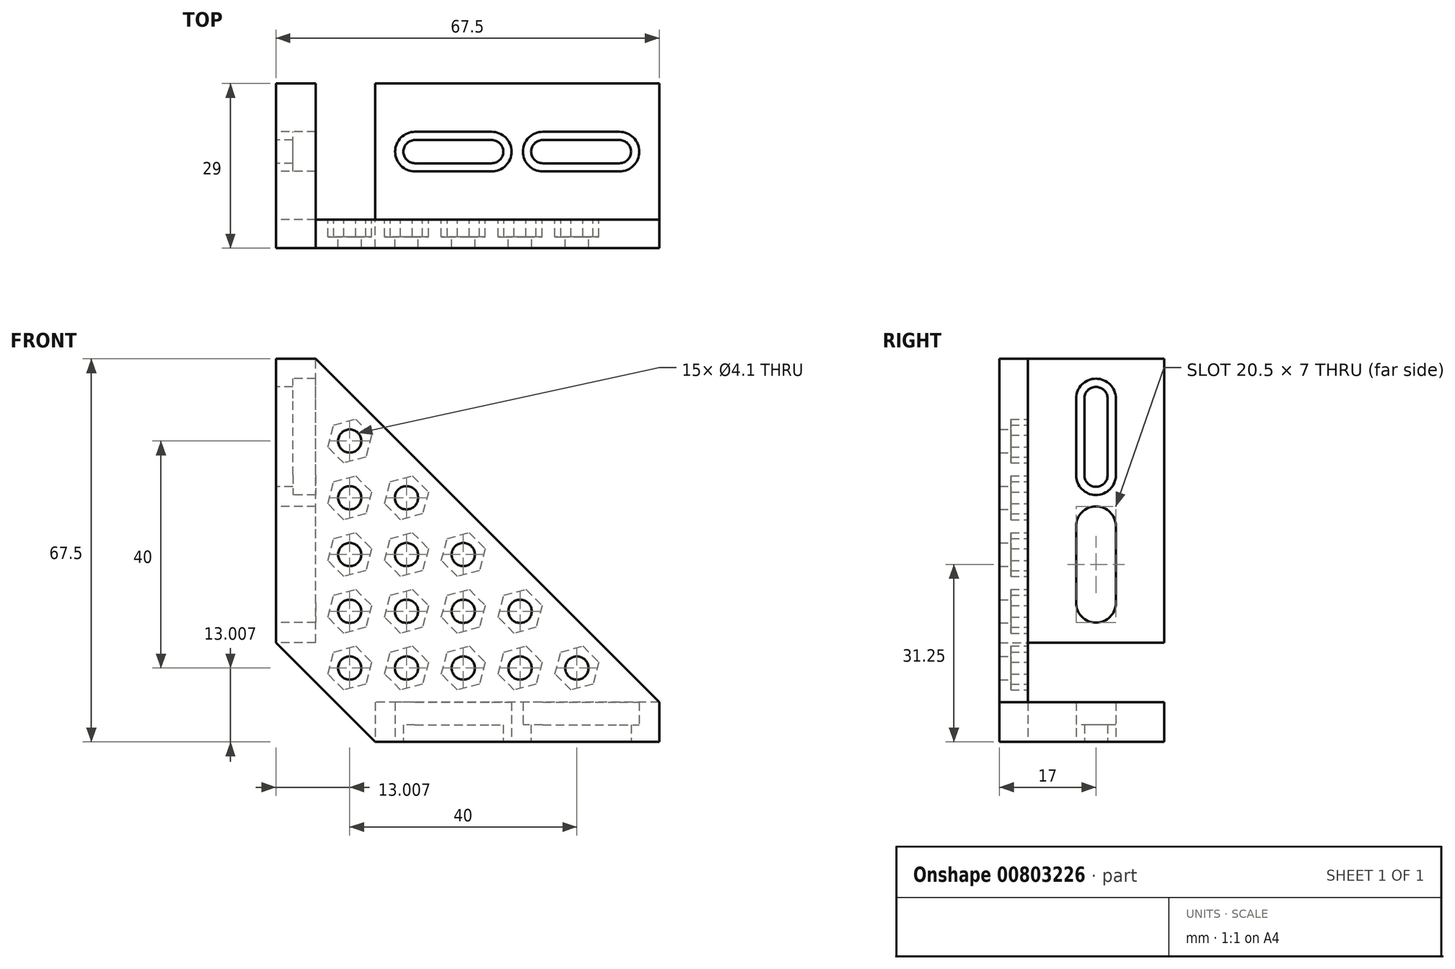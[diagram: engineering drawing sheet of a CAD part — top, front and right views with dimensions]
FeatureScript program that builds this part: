
annotation { "Feature Type Name" : "Feature", "Feature Type Description" : "" }
export const myFeature = defineFeature(function(context is Context, id is Id, definition is map)
    precondition{}
    {
        {
            var Q0;
            Q0=qCreatedBy(makeId("Top.planeOp"),FACE);
            var sketch = newSketch(context, id + "F0", { "sketchPlane" : qUnion([Q0])});
            skLineSegment(sketch, "E0.left", {"start": v(-21, 12) * mm, "end": v(-21, -12) * mm});
            skPoint(sketch, "E0.middle", {"position": v(0, 0) * mm});
            skLineSegment(sketch, "E1", {"start": v(-14, 12) * mm, "end": v(-14, -12) * mm, "construction": true});
            skPoint(sketch, "E2", {"position": v(-14, -8) * mm});
            skPoint(sketch, "E3", {"position": v(0, -8) * mm});
            skPoint(sketch, "E4", {"position": v(-14, 0) * mm});
            skArc(sketch, "E5", {"start": v(-14, -5.95) * mm, "mid": v(-16.05, -8) * mm, "end": v(-14, -10.05) * mm});
            skLineSegment(sketch, "E6", {"start": v(-14, -5.95) * mm, "end": v(0, -5.95) * mm});
            skLineSegment(sketch, "E7.MirrorCS", {"start": v(-14, -10.05) * mm, "end": v(0, -10.05) * mm});
            skArc(sketch, "E8", {"start": v(-14, -2.05) * mm, "mid": v(-16.05, 0) * mm, "end": v(-14, 2.05) * mm});
            skLineSegment(sketch, "E9", {"start": v(-14, -2.05) * mm, "end": v(0, -2.05) * mm});
            skPoint(sketch, "E10.MirrorP", {"position": v(-14, 2.05) * mm});
            skLineSegment(sketch, "E11.MirrorCS", {"start": v(-14, 2.05) * mm, "end": v(0, 2.05) * mm});
            skLineSegment(sketch, "E12.MirrorCS", {"start": v(0, -12) * mm, "end": v(0, 12) * mm, "construction": true});
            skLineSegment(sketch, "E13", {"start": v(-21, -12) * mm, "end": v(0, -12) * mm});
            skLineSegment(sketch, "E14", {"start": v(-21, 0) * mm, "end": v(0, 0) * mm, "construction": true});
            skLineSegment(sketch, "E15", {"start": v(0, -8) * mm, "end": v(-21, -8) * mm, "construction": true});
            skPoint(sketch, "E15.endSnap0", {"position": v(-16.05, -8) * mm});
            skLineSegment(sketch, "E16", {"start": v(0, -12) * mm, "end": v(29, -12) * mm});
            skLineSegment(sketch, "E17", {"start": v(29, -12) * mm, "end": v(29, 12) * mm});
            skLineSegment(sketch, "E18", {"start": v(29, 12) * mm, "end": v(-21, 12) * mm});
            skLineSegment(sketch, "E19", {"start": v(22, 12) * mm, "end": v(22, -12) * mm, "construction": true});
            skLineSegment(sketch, "E20", {"start": v(0, -5.95) * mm, "end": v(22, -5.95) * mm});
            skLineSegment(sketch, "E21", {"start": v(0, -10.05) * mm, "end": v(22, -10.05) * mm});
            skLineSegment(sketch, "E22", {"start": v(22, 0) * mm, "end": v(0, 0) * mm, "construction": true});
            skLineSegment(sketch, "E23", {"start": v(0, -8) * mm, "end": v(22, -8) * mm, "construction": true});
            skArc(sketch, "E24", {"start": v(22, -2.05) * mm, "mid": v(24.05, 0) * mm, "end": v(22, 2.05) * mm});
            skArc(sketch, "E25", {"start": v(22, -10.05) * mm, "mid": v(24.05, -8) * mm, "end": v(22, -5.95) * mm});
            skLineSegment(sketch, "E26.MirrorCS", {"start": v(0, 5.95) * mm, "end": v(22, 5.95) * mm});
            skLineSegment(sketch, "E27.MirrorCS", {"start": v(0, 10.05) * mm, "end": v(22, 10.05) * mm});
            skLineSegment(sketch, "E28.MirrorCS", {"start": v(-14, 10.05) * mm, "end": v(0, 10.05) * mm});
            skLineSegment(sketch, "E29.MirrorCS", {"start": v(-14, 5.95) * mm, "end": v(0, 5.95) * mm});
            skArc(sketch, "E30.MirrorCS", {"start": v(-14, 5.95) * mm, "mid": v(-16.05, 8) * mm, "end": v(-14, 10.05) * mm});
            skArc(sketch, "E31.MirrorCS", {"start": v(22, 10.05) * mm, "mid": v(24.05, 8) * mm, "end": v(22, 5.95) * mm});
            skArc(sketch, "E32.0", {"start": v(-14, -3.5) * mm, "mid": v(-17.5, 0) * mm, "end": v(-14, 3.5) * mm});
            skLineSegment(sketch, "E32.1", {"start": v(2, 3.5) * mm, "end": v(22, 3.5) * mm});
            skArc(sketch, "E32.2", {"start": v(22, -3.5) * mm, "mid": v(25.5, 0) * mm, "end": v(22, 3.5) * mm});
            skLineSegment(sketch, "E32.3", {"start": v(-14, 3.5) * mm, "end": v(2, 3.5) * mm});
            skLineSegment(sketch, "E32.4", {"start": v(2, -3.5) * mm, "end": v(22, -3.5) * mm});
            skLineSegment(sketch, "E32.5", {"start": v(-14, -3.5) * mm, "end": v(2, -3.5) * mm});
            skArc(sketch, "E33.0", {"start": v(-14, -4.5) * mm, "mid": v(-17.5, -8) * mm, "end": v(-14, -11.5) * mm});
            skLineSegment(sketch, "E33.1", {"start": v(2, -4.5) * mm, "end": v(22, -4.5) * mm});
            skArc(sketch, "E33.2", {"start": v(22, -11.5) * mm, "mid": v(25.5, -8) * mm, "end": v(22, -4.5) * mm});
            skLineSegment(sketch, "E33.3", {"start": v(-14, -4.5) * mm, "end": v(2, -4.5) * mm});
            skLineSegment(sketch, "E33.4", {"start": v(2, -11.5) * mm, "end": v(22, -11.5) * mm});
            skLineSegment(sketch, "E33.5", {"start": v(-14, -11.5) * mm, "end": v(2, -11.5) * mm});
            skArc(sketch, "E34.0", {"start": v(-14, 4.5) * mm, "mid": v(-17.5, 8) * mm, "end": v(-14, 11.5) * mm});
            skLineSegment(sketch, "E34.1", {"start": v(0, 11.5) * mm, "end": v(22, 11.5) * mm});
            skArc(sketch, "E34.2", {"start": v(22, 11.5) * mm, "mid": v(25.5, 8) * mm, "end": v(22, 4.5) * mm});
            skLineSegment(sketch, "E34.3", {"start": v(-14, 11.5) * mm, "end": v(0, 11.5) * mm});
            skLineSegment(sketch, "E34.4", {"start": v(0, 4.5) * mm, "end": v(22, 4.5) * mm});
            skLineSegment(sketch, "E34.5", {"start": v(-14, 4.5) * mm, "end": v(0, 4.5) * mm});
            skLineSegment(sketch, "E35", {"start": v(4, 12) * mm, "end": v(4, -12) * mm, "construction": true});
            skPoint(sketch, "E36", {"position": v(-0.5, 0) * mm});
            skPoint(sketch, "E37", {"position": v(8.5, 0) * mm});
            skArc(sketch, "E38", {"start": v(-0.5, -3.5) * mm, "mid": v(3, 0) * mm, "end": v(-0.5, 3.5) * mm});
            skArc(sketch, "E39", {"start": v(-0.5, -2.05) * mm, "mid": v(1.55, 0) * mm, "end": v(-0.5, 2.05) * mm});
            skArc(sketch, "E40", {"start": v(8.5, -3.5) * mm, "mid": v(5, 0) * mm, "end": v(8.5, 3.5) * mm});
            skArc(sketch, "E41", {"start": v(8.5, -2.05) * mm, "mid": v(6.45, 0) * mm, "end": v(8.5, 2.05) * mm});
            skPoint(sketch, "E42", {"position": v(1.55, 0) * mm});
            skPoint(sketch, "E43", {"position": v(3, 0) * mm});
            skPoint(sketch, "E44", {"position": v(5, 0) * mm});
            skPoint(sketch, "E45", {"position": v(6.45, 0) * mm});
            skLineSegment(sketch, "E46", {"start": v(8.5, -2.05) * mm, "end": v(22, -2.05) * mm});
            skLineSegment(sketch, "E47", {"start": v(8.5, 2.05) * mm, "end": v(22, 2.05) * mm});
            skSolve(sketch);
        }
        {
            var Q0;
            Q0=makeQuery(id+"F0.imprint","IMPRINT",FACE,{"disambiguationData":[TD([[makeQuery(id+"F0.imprint","IMPRINT",EDGE,{"derivedFrom":sQuery(id+"F0.wireOp",EDGE,"E0.left")}),1.0]])]});
            var Q1;
            Q1=makeQuery(id+"F0.imprint","IMPRINT",FACE,{"disambiguationData":[TD([[makeQuery(id+"F0.imprint","IMPRINT",EDGE,{"derivedFrom":sQuery(id+"F0.wireOp",EDGE,"E5")}),1.0]])]});
            var Q2;
            Q2=makeQuery(id+"F0.imprint","IMPRINT",FACE,{"disambiguationData":[TD([[makeQuery(id+"F0.imprint","IMPRINT",EDGE,{"derivedFrom":sQuery(id+"F0.wireOp",EDGE,"E5")}),-1.0]])]});
            var Q3;
            Q3=makeQuery(id+"F0.imprint","IMPRINT",FACE,{"disambiguationData":[TD([[makeQuery(id+"F0.imprint","IMPRINT",EDGE,{"derivedFrom":sQuery(id+"F0.wireOp",EDGE,"E26.MirrorCS")}),-1.0]])]});
            var Q4;
            Q4=makeQuery(id+"F0.imprint","IMPRINT",FACE,{"disambiguationData":[TD([[makeQuery(id+"F0.imprint","IMPRINT",EDGE,{"derivedFrom":sQuery(id+"F0.wireOp",EDGE,"E26.MirrorCS")}),1.0]])]});
            var Q5;
            {var subQ3=sQuery(id+"F0.wireOp",EDGE,"E38");Q5=makeQuery(id+"F0.imprint","IMPRINT",FACE,{"disambiguationData":[TD([[makeQuery(id+"F0.imprint","IMPRINT",EDGE,{"derivedFrom":subQ3}),-1.0]])]});}
            extrude(context, id + "F1", {"entities" : qUnion([Q0, Q1, Q2, Q3, Q4, Q5]), "depth" : 7 * mm, "offsetDistance" : 25 * mm});
        }
        {
            var Q0;
            Q0=makeQuery(id+"F0.imprint","IMPRINT",FACE,{"disambiguationData":[TD([[makeQuery(id+"F0.imprint","IMPRINT",EDGE,{"derivedFrom":sQuery(id+"F0.wireOp",EDGE,"E8")}),1.0]])]});
            var Q1;
            Q1=makeQuery(id+"F0.imprint","IMPRINT",FACE,{"disambiguationData":[TD([[makeQuery(id+"F0.imprint","IMPRINT",EDGE,{"derivedFrom":sQuery(id+"F0.wireOp",EDGE,"E24")}),-1.0]])]});
            extrude(context, id + "F2", {"entities" : qUnion([Q0, Q1]), "operationType" : NewBodyOperationType.ADD, "depth" : 3 * mm, "offsetDistance" : 25 * mm});
        }
        {
            var Q0;
            Q0=makeQuery(id+"F1.opExtrude","SWEPT_FACE",FACE,{"disambiguationData":[OSD([sQuery(id+"F0.wireOp",EDGE,"E0.left")])]});
            var sketch = newSketch(context, id + "F3", { "sketchPlane" : qUnion([Q0])});
            skLineSegment(sketch, "E48", {"start": v(-12, 3.5) * mm, "end": v(12, 3.5) * mm, "construction": true});
            skSolve(sketch);
        }
        {
            var Q0;
            Q0=makeQuery(id+"F1.opExtrude","SWEPT_BODY",BODY,{"disambiguationData":[OSD([sQuery(id+"F0.wireOp",EDGE,"E0.bottom"),sQuery(id+"F0.wireOp",EDGE,"E0.top"),sQuery(id+"F0.wireOp",EDGE,"E0.left"),sQuery(id+"F0.wireOp",EDGE,"E0.right"),sQuery(id+"F0.wireOp",EDGE,"rf366HtQ-3S43-huQP-rZQL-GLvETnePYKPt"),sQuery(id+"F0.wireOp",EDGE,"72d57c59-205e-4b86-9b7f-fefa83471a3c0.MirrorC"),sQuery(id+"F0.wireOp",EDGE,"3BxVGwLA-TLUy-tZVP-cH0U-NxRYkcQ5ksQi"),sQuery(id+"F0.wireOp",EDGE,"b526d6a5-a937-4610-9a53-f8e406b30c9d0.MirrorC"),sQuery(id+"F0.wireOp",EDGE,"71981b63-6e51-433c-862b-60b74b25135c0.MirrorC"),sQuery(id+"F0.wireOp",EDGE,"b5f8f83e-67df-48da-9f18-6f8bbd20fa1b0.MirrorC"),sQuery(id+"F0.wireOp",EDGE,"1DxgEhBs-8iCY-IMLj-HmtB-05ri525AO9wY"),sQuery(id+"F0.wireOp",EDGE,"NxLUD5A4-VjtB-lD8M-x3iM-VxBEk0lLSaKk"),sQuery(id+"F0.wireOp",EDGE,"3f1f5e11-1e70-4af8-87df-d7b5c765f6460.MirrorC")])]});
            var Q1;
            Q1=sQuery(id+"F3.wireOp",EDGE,"E48");
            transform(context, id + "F4", {"entities" : qUnion([Q0]), "transformType" : TransformType.ROTATION, "transformAxis" : qUnion([Q1]), "angle" : 90 * degree, "makeCopy" : true});
        }
        {
            var Q0;
            Q0=makeQuery(id+"F4.opPattern","COPY",FACE,{"derivedFrom":makeQuery(id+"F1.opExtrude","SWEPT_FACE",FACE,{"disambiguationData":[OSD([sQuery(id+"F0.wireOp",EDGE,"E0.left")])]}),"instanceName":"1"});
            var sketch = newSketch(context, id + "F5", { "sketchPlane" : qUnion([Q0])});
            skLineSegment(sketch, "E49", {"start": v(-21, -12) * mm, "end": v(-21, 12) * mm, "construction": true});
            skPoint(sketch, "E49.startSnap0", {"position": v(-21, -12) * mm});
            skSolve(sketch);
        }
        {
            var Q0;
            Q0=sQuery(id+"F5.wireOp",EDGE,"E49");
            cPlane(context, id + "F6", {"entities" : qUnion([Q0]), "cplaneType" : CPlaneType.LINE_ANGLE, "offset" : 25 * mm, "angle" : 90 * degree, "width" : 150 * mm, "height" : 150 * mm});
        }
        {
            var Q0;
            Q0=qCreatedBy(id+"F6.planeOp",FACE);
            var sketch = newSketch(context, id + "F7", { "sketchPlane" : qUnion([Q0])});
            skLineSegment(sketch, "E50", {"start": v(0, 3.5) * mm, "end": v(0, 53.5) * mm, "construction": true});
            skSolve(sketch);
        }
        {
            var Q0;
            Q0=makeQuery(id+"F4.opPattern","COPY",BODY,{"derivedFrom":makeQuery(id+"F1.opExtrude","SWEPT_BODY",BODY,{"disambiguationData":[OSD([sQuery(id+"F0.wireOp",EDGE,"E0.left"),sQuery(id+"F0.wireOp",EDGE,"E13"),sQuery(id+"F0.wireOp",EDGE,"E16"),sQuery(id+"F0.wireOp",EDGE,"E17"),sQuery(id+"F0.wireOp",EDGE,"E18"),sQuery(id+"F0.wireOp",EDGE,"E32.0"),sQuery(id+"F0.wireOp",EDGE,"E32.1"),sQuery(id+"F0.wireOp",EDGE,"E32.2"),sQuery(id+"F0.wireOp",EDGE,"E32.3"),sQuery(id+"F0.wireOp",EDGE,"E32.4"),sQuery(id+"F0.wireOp",EDGE,"E32.5")])]}),"instanceName":"1"});
            var Q1;
            Q1=sQuery(id+"F7.wireOp",EDGE,"E50");
            transform(context, id + "F8", {"entities" : qUnion([Q0]), "transformType" : TransformType.ROTATION, "transformAxis" : qUnion([Q1]), "angle" : 180 * degree, "makeCopy" : false});
        }
        {
            var Q0;
            Q0=makeQuery(id+"F4.opPattern","COPY",BODY,{"derivedFrom":makeQuery(id+"F1.opExtrude","SWEPT_BODY",BODY,{"disambiguationData":[OSD([sQuery(id+"F0.wireOp",EDGE,"E0.bottom"),sQuery(id+"F0.wireOp",EDGE,"E0.top"),sQuery(id+"F0.wireOp",EDGE,"E0.left"),sQuery(id+"F0.wireOp",EDGE,"E0.right"),sQuery(id+"F0.wireOp",EDGE,"rf366HtQ-3S43-huQP-rZQL-GLvETnePYKPt"),sQuery(id+"F0.wireOp",EDGE,"72d57c59-205e-4b86-9b7f-fefa83471a3c0.MirrorC"),sQuery(id+"F0.wireOp",EDGE,"3BxVGwLA-TLUy-tZVP-cH0U-NxRYkcQ5ksQi"),sQuery(id+"F0.wireOp",EDGE,"b526d6a5-a937-4610-9a53-f8e406b30c9d0.MirrorC"),sQuery(id+"F0.wireOp",EDGE,"71981b63-6e51-433c-862b-60b74b25135c0.MirrorC"),sQuery(id+"F0.wireOp",EDGE,"b5f8f83e-67df-48da-9f18-6f8bbd20fa1b0.MirrorC"),sQuery(id+"F0.wireOp",EDGE,"1DxgEhBs-8iCY-IMLj-HmtB-05ri525AO9wY"),sQuery(id+"F0.wireOp",EDGE,"NxLUD5A4-VjtB-lD8M-x3iM-VxBEk0lLSaKk"),sQuery(id+"F0.wireOp",EDGE,"3f1f5e11-1e70-4af8-87df-d7b5c765f6460.MirrorC")])]}),"instanceName":"1"});
            var Q1;
            Q1=qCreatedBy(makeId("Top.planeOp"),FACE);
            transform(context, id + "F9", {"entities" : qUnion([Q0]), "transformType" : TransformType.TRANSLATION_DISTANCE, "transformDirection" : qUnion([Q1]), "distance" : 14 * mm, "makeCopy" : false});
        }
        {
            var Q0;
            Q0=makeQuery(id+"F4.opPattern","COPY",BODY,{"derivedFrom":makeQuery(id+"F1.opExtrude","SWEPT_BODY",BODY,{"disambiguationData":[OSD([sQuery(id+"F0.wireOp",EDGE,"E0.bottom"),sQuery(id+"F0.wireOp",EDGE,"E0.top"),sQuery(id+"F0.wireOp",EDGE,"E0.left"),sQuery(id+"F0.wireOp",EDGE,"E0.right"),sQuery(id+"F0.wireOp",EDGE,"rf366HtQ-3S43-huQP-rZQL-GLvETnePYKPt"),sQuery(id+"F0.wireOp",EDGE,"72d57c59-205e-4b86-9b7f-fefa83471a3c0.MirrorC"),sQuery(id+"F0.wireOp",EDGE,"3BxVGwLA-TLUy-tZVP-cH0U-NxRYkcQ5ksQi"),sQuery(id+"F0.wireOp",EDGE,"b526d6a5-a937-4610-9a53-f8e406b30c9d0.MirrorC"),sQuery(id+"F0.wireOp",EDGE,"71981b63-6e51-433c-862b-60b74b25135c0.MirrorC"),sQuery(id+"F0.wireOp",EDGE,"b5f8f83e-67df-48da-9f18-6f8bbd20fa1b0.MirrorC"),sQuery(id+"F0.wireOp",EDGE,"1DxgEhBs-8iCY-IMLj-HmtB-05ri525AO9wY"),sQuery(id+"F0.wireOp",EDGE,"NxLUD5A4-VjtB-lD8M-x3iM-VxBEk0lLSaKk"),sQuery(id+"F0.wireOp",EDGE,"3f1f5e11-1e70-4af8-87df-d7b5c765f6460.MirrorC")])]}),"instanceName":"1"});
            var Q1;
            Q1=qCreatedBy(makeId("Right.planeOp"),FACE);
            transform(context, id + "F10", {"entities" : qUnion([Q0]), "transformType" : TransformType.TRANSLATION_DISTANCE, "transformDirection" : qUnion([Q1]), "distance" : 14 * mm, "oppositeDirection" : true, "makeCopy" : false});
        }
        {
            var Q0;
            Q0=sQuery(id+"F0.wireOp",VERTEX,"E0.left.end");
            var Q1;
            Q1=makeQuery(id+"F4.opPattern","COPY",VERTEX,{"derivedFrom":makeQuery(id+"F1.opExtrude","CAP_VERTEX",VERTEX,{"disambiguationData":[OSD([sQuery(id+"F0.wireOp",EDGE,"E0.left"),sQuery(id+"F0.wireOp",EDGE,"E18")])],"isStart":true}),"instanceName":"1"});
            var Q2;
            Q2=makeQuery(id+"F4.opPattern","COPY",VERTEX,{"derivedFrom":makeQuery(id+"F1.opExtrude","CAP_VERTEX",VERTEX,{"disambiguationData":[OSD([sQuery(id+"F0.wireOp",EDGE,"E0.left"),sQuery(id+"F0.wireOp",EDGE,"E18")])],"isStart":false}),"instanceName":"1"});
            cPlane(context, id + "F11", {"entities" : qUnion([Q0, Q1, Q2]), "cplaneType" : CPlaneType.THREE_POINT, "offset" : 25 * mm, "width" : 150 * mm, "height" : 150 * mm});
        }
        {
            var Q0;
            Q0=qCreatedBy(id+"F11.planeOp",FACE);
            var sketch = newSketch(context, id + "F12", { "sketchPlane" : qUnion([Q0])});
            skLineSegment(sketch, "E51", {"start": v(-21, 0) * mm, "end": v(-38.5, 17.5) * mm});
            skLineSegment(sketch, "E52", {"start": v(-31.5, 67.5) * mm, "end": v(29, 7) * mm});
            skLineSegment(sketch, "E53", {"start": v(-38.5, 17.5) * mm, "end": v(-38.5, 67.5) * mm});
            skLineSegment(sketch, "E54", {"start": v(-31.5, 67.5) * mm, "end": v(-38.5, 67.5) * mm});
            skLineSegment(sketch, "E55", {"start": v(-21, 0) * mm, "end": v(29, 0) * mm});
            skLineSegment(sketch, "E56", {"start": v(29, 0) * mm, "end": v(29, 7) * mm});
            skLineSegment(sketch, "E57", {"start": v(-38.5, 67.5) * mm, "end": v(-31.5, 67.5) * mm});
            skPoint(sketch, "E58", {"position": v(-5.5, 33) * mm});
            skCircle(sketch, "E59", {"center": v(-5.5, 33) * mm, "radius": 2.05 * mm});
            skCircle(sketch, "E60.cCircle", {"center": v(-5.5, 33) * mm, "radius": 4 * mm, "construction": true});
            skLineSegment(sketch, "E60.0", {"start": v(-8.32, 35.84) * mm, "end": v(-4.46, 36.87) * mm});
            skLineSegment(sketch, "E60.1", {"start": v(-4.46, 36.87) * mm, "end": v(-1.63, 34.04) * mm});
            skLineSegment(sketch, "E60.2", {"start": v(-1.63, 34.04) * mm, "end": v(-2.66, 30.18) * mm});
            skLineSegment(sketch, "E60.3", {"start": v(-2.66, 30.18) * mm, "end": v(-6.53, 29.14) * mm});
            skLineSegment(sketch, "E60.4", {"start": v(-6.53, 29.14) * mm, "end": v(-9.36, 31.97) * mm});
            skLineSegment(sketch, "E60.5", {"start": v(-9.36, 31.97) * mm, "end": v(-8.32, 35.84) * mm});
            skLineSegment(sketch, "E61", {"start": v(-29.75, 8.75) * mm, "end": v(-1.25, 37.25) * mm, "construction": true});
            skLineSegment(sketch, "E62", {"start": v(-38.5, 17.5) * mm, "end": v(-38.5, 0) * mm, "construction": true});
            skLineSegment(sketch, "E63", {"start": v(-38.5, 0) * mm, "end": v(-21, 0) * mm, "construction": true});
            skLineSegment(sketch, "E64", {"start": v(-21, 7) * mm, "end": v(-38.5, 7) * mm, "construction": true});
            skLineSegment(sketch, "E65", {"start": v(-38.5, 7) * mm, "end": v(-38.5, 17.5) * mm, "construction": true});
            skLineSegment(sketch, "E66", {"start": v(-23.5, 59.5) * mm, "end": v(-23.5, 15) * mm, "construction": true});
            skLineSegment(sketch, "E67", {"start": v(-23.5, 15) * mm, "end": v(21, 15) * mm, "construction": true});
            skPoint(sketch, "E68", {"position": v(-2.66, 35.84) * mm});
            skLineSegment(sketch, "E69", {"start": v(-5.5, 33) * mm, "end": v(-5.5, 15) * mm, "construction": true});
            skLineSegment(sketch, "E70", {"start": v(-5.5, 33) * mm, "end": v(-23.5, 33) * mm, "construction": true});
            skPoint(sketch, "E71", {"position": v(-5.5, 23) * mm});
            skCircle(sketch, "E72", {"center": v(-5.5, 23) * mm, "radius": 2.05 * mm});
            skCircle(sketch, "E73.cCircle", {"center": v(-5.5, 23) * mm, "radius": 4 * mm, "construction": true});
            skLineSegment(sketch, "E73.0", {"start": v(-8.32, 25.84) * mm, "end": v(-4.46, 26.87) * mm});
            skLineSegment(sketch, "E73.1", {"start": v(-4.46, 26.87) * mm, "end": v(-1.63, 24.04) * mm});
            skLineSegment(sketch, "E73.2", {"start": v(-1.63, 24.04) * mm, "end": v(-2.66, 20.18) * mm});
            skLineSegment(sketch, "E73.3", {"start": v(-2.66, 20.18) * mm, "end": v(-6.53, 19.14) * mm});
            skLineSegment(sketch, "E73.4", {"start": v(-6.53, 19.14) * mm, "end": v(-9.36, 21.97) * mm});
            skLineSegment(sketch, "E73.5", {"start": v(-9.36, 21.97) * mm, "end": v(-8.32, 25.84) * mm});
            skPoint(sketch, "E74", {"position": v(-15.5, 33) * mm});
            skCircle(sketch, "E75", {"center": v(-15.5, 33) * mm, "radius": 2.05 * mm});
            skCircle(sketch, "E76.cCircle", {"center": v(-15.5, 33) * mm, "radius": 4 * mm, "construction": true});
            skLineSegment(sketch, "E76.0", {"start": v(-18.32, 35.84) * mm, "end": v(-14.46, 36.87) * mm});
            skLineSegment(sketch, "E76.1", {"start": v(-14.46, 36.87) * mm, "end": v(-11.63, 34.04) * mm});
            skLineSegment(sketch, "E76.2", {"start": v(-11.63, 34.04) * mm, "end": v(-12.66, 30.18) * mm});
            skLineSegment(sketch, "E76.3", {"start": v(-12.66, 30.18) * mm, "end": v(-16.53, 29.14) * mm});
            skLineSegment(sketch, "E76.4", {"start": v(-16.53, 29.14) * mm, "end": v(-19.36, 31.97) * mm});
            skLineSegment(sketch, "E76.5", {"start": v(-19.36, 31.97) * mm, "end": v(-18.32, 35.84) * mm});
            skPoint(sketch, "E77", {"position": v(-15.5, 23) * mm});
            skCircle(sketch, "E78", {"center": v(-15.5, 23) * mm, "radius": 2.05 * mm});
            skCircle(sketch, "E79.cCircle", {"center": v(-15.5, 23) * mm, "radius": 4 * mm, "construction": true});
            skLineSegment(sketch, "E79.0", {"start": v(-18.32, 25.84) * mm, "end": v(-14.46, 26.87) * mm});
            skLineSegment(sketch, "E79.1", {"start": v(-14.46, 26.87) * mm, "end": v(-11.63, 24.04) * mm});
            skLineSegment(sketch, "E79.2", {"start": v(-11.63, 24.04) * mm, "end": v(-12.66, 20.18) * mm});
            skLineSegment(sketch, "E79.3", {"start": v(-12.66, 20.18) * mm, "end": v(-16.53, 19.14) * mm});
            skLineSegment(sketch, "E79.4", {"start": v(-16.53, 19.14) * mm, "end": v(-19.36, 21.97) * mm});
            skLineSegment(sketch, "E79.5", {"start": v(-19.36, 21.97) * mm, "end": v(-18.32, 25.84) * mm});
            skLineSegment(sketch, "E80", {"start": v(-5.5, 23) * mm, "end": v(13, 23) * mm, "construction": true});
            skLineSegment(sketch, "E81", {"start": v(-15.5, 33) * mm, "end": v(-15.5, 51.5) * mm, "construction": true});
            skPoint(sketch, "E82", {"position": v(4.5, 23) * mm});
            skCircle(sketch, "E83", {"center": v(4.5, 23) * mm, "radius": 2.05 * mm});
            skCircle(sketch, "E84.cCircle", {"center": v(4.5, 23) * mm, "radius": 4 * mm, "construction": true});
            skLineSegment(sketch, "E84.0", {"start": v(1.68, 25.84) * mm, "end": v(5.54, 26.87) * mm});
            skLineSegment(sketch, "E84.1", {"start": v(5.54, 26.87) * mm, "end": v(8.37, 24.04) * mm});
            skLineSegment(sketch, "E84.2", {"start": v(8.37, 24.04) * mm, "end": v(7.34, 20.18) * mm});
            skLineSegment(sketch, "E84.3", {"start": v(7.34, 20.18) * mm, "end": v(3.47, 19.14) * mm});
            skLineSegment(sketch, "E84.4", {"start": v(3.47, 19.14) * mm, "end": v(0.64, 21.97) * mm});
            skLineSegment(sketch, "E84.5", {"start": v(0.64, 21.97) * mm, "end": v(1.68, 25.84) * mm});
            skPoint(sketch, "E85", {"position": v(-15.5, 43) * mm});
            skCircle(sketch, "E86", {"center": v(-15.5, 43) * mm, "radius": 2.05 * mm});
            skCircle(sketch, "E87.cCircle", {"center": v(-15.5, 43) * mm, "radius": 4 * mm, "construction": true});
            skLineSegment(sketch, "E87.0", {"start": v(-18.32, 45.84) * mm, "end": v(-14.46, 46.87) * mm});
            skLineSegment(sketch, "E87.1", {"start": v(-14.46, 46.87) * mm, "end": v(-11.63, 44.04) * mm});
            skLineSegment(sketch, "E87.2", {"start": v(-11.63, 44.04) * mm, "end": v(-12.66, 40.18) * mm});
            skLineSegment(sketch, "E87.3", {"start": v(-12.66, 40.18) * mm, "end": v(-16.53, 39.14) * mm});
            skLineSegment(sketch, "E87.4", {"start": v(-16.53, 39.14) * mm, "end": v(-19.36, 41.97) * mm});
            skLineSegment(sketch, "E87.5", {"start": v(-19.36, 41.97) * mm, "end": v(-18.32, 45.84) * mm});
            skPoint(sketch, "E88", {"position": v(-25.5, 33) * mm});
            skCircle(sketch, "E89", {"center": v(-25.5, 33) * mm, "radius": 2.05 * mm});
            skCircle(sketch, "E90.cCircle", {"center": v(-25.5, 33) * mm, "radius": 4 * mm, "construction": true});
            skLineSegment(sketch, "E90.0", {"start": v(-28.32, 35.84) * mm, "end": v(-24.46, 36.87) * mm});
            skLineSegment(sketch, "E90.1", {"start": v(-24.46, 36.87) * mm, "end": v(-21.63, 34.04) * mm});
            skLineSegment(sketch, "E90.2", {"start": v(-21.63, 34.04) * mm, "end": v(-22.66, 30.18) * mm});
            skLineSegment(sketch, "E90.3", {"start": v(-22.66, 30.18) * mm, "end": v(-26.53, 29.14) * mm});
            skLineSegment(sketch, "E90.4", {"start": v(-26.53, 29.14) * mm, "end": v(-29.36, 31.97) * mm});
            skLineSegment(sketch, "E90.5", {"start": v(-29.36, 31.97) * mm, "end": v(-28.32, 35.84) * mm});
            skPoint(sketch, "E91", {"position": v(-25.5, 23) * mm});
            skCircle(sketch, "E92", {"center": v(-25.5, 23) * mm, "radius": 2.05 * mm});
            skCircle(sketch, "E93.cCircle", {"center": v(-25.5, 23) * mm, "radius": 4 * mm, "construction": true});
            skLineSegment(sketch, "E93.0", {"start": v(-28.32, 25.84) * mm, "end": v(-24.46, 26.87) * mm});
            skLineSegment(sketch, "E93.1", {"start": v(-24.46, 26.87) * mm, "end": v(-21.63, 24.04) * mm});
            skLineSegment(sketch, "E93.2", {"start": v(-21.63, 24.04) * mm, "end": v(-22.66, 20.18) * mm});
            skLineSegment(sketch, "E93.3", {"start": v(-22.66, 20.18) * mm, "end": v(-26.53, 19.14) * mm});
            skLineSegment(sketch, "E93.4", {"start": v(-26.53, 19.14) * mm, "end": v(-29.36, 21.97) * mm});
            skLineSegment(sketch, "E93.5", {"start": v(-29.36, 21.97) * mm, "end": v(-28.32, 25.84) * mm});
            skPoint(sketch, "E94", {"position": v(-25.5, 43) * mm});
            skCircle(sketch, "E95", {"center": v(-25.5, 43) * mm, "radius": 2.05 * mm});
            skCircle(sketch, "E96.cCircle", {"center": v(-25.5, 43) * mm, "radius": 4 * mm, "construction": true});
            skLineSegment(sketch, "E96.0", {"start": v(-28.32, 45.84) * mm, "end": v(-24.46, 46.87) * mm});
            skLineSegment(sketch, "E96.1", {"start": v(-24.46, 46.87) * mm, "end": v(-21.63, 44.04) * mm});
            skLineSegment(sketch, "E96.2", {"start": v(-21.63, 44.04) * mm, "end": v(-22.66, 40.18) * mm});
            skLineSegment(sketch, "E96.3", {"start": v(-22.66, 40.18) * mm, "end": v(-26.53, 39.14) * mm});
            skLineSegment(sketch, "E96.4", {"start": v(-26.53, 39.14) * mm, "end": v(-29.36, 41.97) * mm});
            skLineSegment(sketch, "E96.5", {"start": v(-29.36, 41.97) * mm, "end": v(-28.32, 45.84) * mm});
            skLineSegment(sketch, "E97", {"start": v(-25.5, 61.5) * mm, "end": v(-25.5, 13) * mm, "construction": true});
            skPoint(sketch, "E98", {"position": v(-5.5, 13) * mm});
            skCircle(sketch, "E99", {"center": v(-5.5, 13) * mm, "radius": 2.05 * mm});
            skCircle(sketch, "E100.cCircle", {"center": v(-5.5, 13) * mm, "radius": 4 * mm, "construction": true});
            skLineSegment(sketch, "E100.0", {"start": v(-8.32, 15.84) * mm, "end": v(-4.46, 16.87) * mm});
            skLineSegment(sketch, "E100.1", {"start": v(-4.46, 16.87) * mm, "end": v(-1.63, 14.04) * mm});
            skLineSegment(sketch, "E100.2", {"start": v(-1.63, 14.04) * mm, "end": v(-2.66, 10.18) * mm});
            skLineSegment(sketch, "E100.3", {"start": v(-2.66, 10.18) * mm, "end": v(-6.53, 9.14) * mm});
            skLineSegment(sketch, "E100.4", {"start": v(-6.53, 9.14) * mm, "end": v(-9.36, 11.97) * mm});
            skLineSegment(sketch, "E100.5", {"start": v(-9.36, 11.97) * mm, "end": v(-8.32, 15.84) * mm});
            skPoint(sketch, "E101", {"position": v(-15.5, 13) * mm});
            skCircle(sketch, "E102", {"center": v(-15.5, 13) * mm, "radius": 2.05 * mm});
            skCircle(sketch, "E103.cCircle", {"center": v(-15.5, 13) * mm, "radius": 4 * mm, "construction": true});
            skLineSegment(sketch, "E103.0", {"start": v(-18.32, 15.84) * mm, "end": v(-14.46, 16.87) * mm});
            skLineSegment(sketch, "E103.1", {"start": v(-14.46, 16.87) * mm, "end": v(-11.63, 14.04) * mm});
            skLineSegment(sketch, "E103.2", {"start": v(-11.63, 14.04) * mm, "end": v(-12.66, 10.18) * mm});
            skLineSegment(sketch, "E103.3", {"start": v(-12.66, 10.18) * mm, "end": v(-16.53, 9.14) * mm});
            skLineSegment(sketch, "E103.4", {"start": v(-16.53, 9.14) * mm, "end": v(-19.36, 11.97) * mm});
            skLineSegment(sketch, "E103.5", {"start": v(-19.36, 11.97) * mm, "end": v(-18.32, 15.84) * mm});
            skPoint(sketch, "E104", {"position": v(4.5, 13) * mm});
            skCircle(sketch, "E105", {"center": v(4.5, 13) * mm, "radius": 2.05 * mm});
            skCircle(sketch, "E106.cCircle", {"center": v(4.5, 13) * mm, "radius": 4 * mm, "construction": true});
            skLineSegment(sketch, "E106.0", {"start": v(1.68, 15.84) * mm, "end": v(5.54, 16.87) * mm});
            skLineSegment(sketch, "E106.1", {"start": v(5.54, 16.87) * mm, "end": v(8.37, 14.04) * mm});
            skLineSegment(sketch, "E106.2", {"start": v(8.37, 14.04) * mm, "end": v(7.34, 10.18) * mm});
            skLineSegment(sketch, "E106.3", {"start": v(7.34, 10.18) * mm, "end": v(3.47, 9.14) * mm});
            skLineSegment(sketch, "E106.4", {"start": v(3.47, 9.14) * mm, "end": v(0.64, 11.97) * mm});
            skLineSegment(sketch, "E106.5", {"start": v(0.64, 11.97) * mm, "end": v(1.68, 15.84) * mm});
            skPoint(sketch, "E107", {"position": v(-25.5, 13) * mm});
            skCircle(sketch, "E108", {"center": v(-25.5, 13) * mm, "radius": 2.05 * mm});
            skCircle(sketch, "E109.cCircle", {"center": v(-25.5, 13) * mm, "radius": 4 * mm, "construction": true});
            skLineSegment(sketch, "E109.0", {"start": v(-28.32, 15.84) * mm, "end": v(-24.46, 16.87) * mm});
            skLineSegment(sketch, "E109.1", {"start": v(-24.46, 16.87) * mm, "end": v(-21.63, 14.04) * mm});
            skLineSegment(sketch, "E109.2", {"start": v(-21.63, 14.04) * mm, "end": v(-22.66, 10.18) * mm});
            skLineSegment(sketch, "E109.3", {"start": v(-22.66, 10.18) * mm, "end": v(-26.53, 9.14) * mm});
            skLineSegment(sketch, "E109.4", {"start": v(-26.53, 9.14) * mm, "end": v(-29.36, 11.97) * mm});
            skLineSegment(sketch, "E109.5", {"start": v(-29.36, 11.97) * mm, "end": v(-28.32, 15.84) * mm});
            skLineSegment(sketch, "E110", {"start": v(23, 13) * mm, "end": v(-25.5, 13) * mm, "construction": true});
            skPoint(sketch, "E111", {"position": v(-25.5, 53) * mm});
            skCircle(sketch, "E112", {"center": v(-25.5, 53) * mm, "radius": 2.05 * mm});
            skCircle(sketch, "E113.cCircle", {"center": v(-25.5, 53) * mm, "radius": 4 * mm, "construction": true});
            skLineSegment(sketch, "E113.0", {"start": v(-29.36, 51.97) * mm, "end": v(-28.32, 55.84) * mm});
            skLineSegment(sketch, "E113.1", {"start": v(-28.32, 55.84) * mm, "end": v(-24.46, 56.87) * mm});
            skLineSegment(sketch, "E113.2", {"start": v(-24.46, 56.87) * mm, "end": v(-21.63, 54.04) * mm});
            skLineSegment(sketch, "E113.3", {"start": v(-21.63, 54.04) * mm, "end": v(-22.66, 50.18) * mm});
            skLineSegment(sketch, "E113.4", {"start": v(-22.66, 50.18) * mm, "end": v(-26.53, 49.14) * mm});
            skLineSegment(sketch, "E113.5", {"start": v(-26.53, 49.14) * mm, "end": v(-29.36, 51.97) * mm});
            skPoint(sketch, "E114", {"position": v(14.5, 13) * mm});
            skCircle(sketch, "E115", {"center": v(14.5, 13) * mm, "radius": 2.05 * mm});
            skCircle(sketch, "E116.cCircle", {"center": v(14.5, 13) * mm, "radius": 4 * mm, "construction": true});
            skLineSegment(sketch, "E116.0", {"start": v(11.68, 15.84) * mm, "end": v(15.54, 16.87) * mm});
            skLineSegment(sketch, "E116.1", {"start": v(15.54, 16.87) * mm, "end": v(18.37, 14.04) * mm});
            skLineSegment(sketch, "E116.2", {"start": v(18.37, 14.04) * mm, "end": v(17.34, 10.18) * mm});
            skLineSegment(sketch, "E116.3", {"start": v(17.34, 10.18) * mm, "end": v(13.47, 9.14) * mm});
            skLineSegment(sketch, "E116.4", {"start": v(13.47, 9.14) * mm, "end": v(10.64, 11.97) * mm});
            skLineSegment(sketch, "E116.5", {"start": v(10.64, 11.97) * mm, "end": v(11.68, 15.84) * mm});
            skSolve(sketch);
        }
        {
            var Q0;
            Q0=makeQuery(id+"F12.imprint","IMPRINT",FACE,{"disambiguationData":[TD([[makeQuery(id+"F12.imprint","IMPRINT",EDGE,{"derivedFrom":sQuery(id+"F12.wireOp",EDGE,"E52")}),-1.0]])]});
            var Q1;
            Q1=makeQuery(id+"F12.imprint","IMPRINT",FACE,{"disambiguationData":[TD([[makeQuery(id+"F12.imprint","IMPRINT",EDGE,{"derivedFrom":sQuery(id+"F12.wireOp",EDGE,"544cc5c5-56e9-462e-aa7d-0e891712fb88")}),-1.0]])]});
            var Q2;
            Q2=makeQuery(id+"F12.imprint","IMPRINT",FACE,{"disambiguationData":[TD([[makeQuery(id+"F12.imprint","IMPRINT",EDGE,{"derivedFrom":sQuery(id+"F12.wireOp",EDGE,"af930993-f983-4d4b-806c-d5d714f01deb")}),-1.0]])]});
            var Q3;
            Q3=makeQuery(id+"F12.imprint","IMPRINT",FACE,{"disambiguationData":[TD([[makeQuery(id+"F12.imprint","IMPRINT",EDGE,{"derivedFrom":sQuery(id+"F12.wireOp",EDGE,"E59")}),-1.0]])]});
            var Q4;
            Q4=makeQuery(id+"F12.imprint","IMPRINT",FACE,{"disambiguationData":[TD([[makeQuery(id+"F12.imprint","IMPRINT",EDGE,{"derivedFrom":sQuery(id+"F12.wireOp",EDGE,"db4000d2-28b7-4ce0-b6f8-efe2c8e47721")}),-1.0]])]});
            var Q5;
            Q5=makeQuery(id+"F12.imprint","IMPRINT",FACE,{"disambiguationData":[TD([[makeQuery(id+"F12.imprint","IMPRINT",EDGE,{"derivedFrom":sQuery(id+"F12.wireOp",EDGE,"6fd45c98-9014-41e2-a4b9-07c20c1fc8f4")}),-1.0]])]});
            var Q6;
            {var subQ0=sQuery(id+"F12.wireOp",EDGE,"36f95dd1-a930-4b05-802e-2328d4aa170c.1");Q6=makeQuery(id+"F12.imprint","IMPRINT",FACE,{"disambiguationData":[TD([[makeQuery(id+"F12.imprint","IMPRINT",EDGE,{"derivedFrom":subQ0}),-1.0]])]});}
            var Q7;
            Q7=makeQuery(id+"F12.imprint","IMPRINT",FACE,{"disambiguationData":[TD([[makeQuery(id+"F12.imprint","IMPRINT",EDGE,{"derivedFrom":sQuery(id+"F12.wireOp",EDGE,"0217be3f-f015-4376-87de-3fac7a7125e00.MirrorCS")}),1.0]])]});
            var Q8;
            Q8=makeQuery(id+"F12.imprint","IMPRINT",FACE,{"disambiguationData":[TD([[makeQuery(id+"F12.imprint","IMPRINT",EDGE,{"derivedFrom":sQuery(id+"F12.wireOp",EDGE,"3a05cbfe-0b2f-41ad-9fce-b7c3e8f461170.MirrorCS")}),1.0]])]});
            var Q9;
            Q9=makeQuery(id+"F12.imprint","IMPRINT",FACE,{"disambiguationData":[TD([[makeQuery(id+"F12.imprint","IMPRINT",EDGE,{"derivedFrom":sQuery(id+"F12.wireOp",EDGE,"686798c7-8504-4800-9966-571d6854760d0.MirrorCS")}),1.0]])]});
            var Q10;
            Q10=makeQuery(id+"F12.imprint","IMPRINT",FACE,{"disambiguationData":[TD([[makeQuery(id+"F12.imprint","IMPRINT",EDGE,{"derivedFrom":sQuery(id+"F12.wireOp",EDGE,"ee1293b9-60a1-4feb-baa6-848b5ec06ea80.MirrorCS")}),1.0]])]});
            var Q11;
            Q11=makeQuery(id+"F12.imprint","IMPRINT",FACE,{"disambiguationData":[TD([[makeQuery(id+"F12.imprint","IMPRINT",EDGE,{"derivedFrom":sQuery(id+"F12.wireOp",EDGE,"E86")}),-1.0]])]});
            var Q12;
            Q12=makeQuery(id+"F12.imprint","IMPRINT",FACE,{"disambiguationData":[TD([[makeQuery(id+"F12.imprint","IMPRINT",EDGE,{"derivedFrom":sQuery(id+"F12.wireOp",EDGE,"E75")}),-1.0]])]});
            var Q13;
            Q13=makeQuery(id+"F12.imprint","IMPRINT",FACE,{"disambiguationData":[TD([[makeQuery(id+"F12.imprint","IMPRINT",EDGE,{"derivedFrom":sQuery(id+"F12.wireOp",EDGE,"E78")}),-1.0]])]});
            var Q14;
            Q14=makeQuery(id+"F12.imprint","IMPRINT",FACE,{"disambiguationData":[TD([[makeQuery(id+"F12.imprint","IMPRINT",EDGE,{"derivedFrom":sQuery(id+"F12.wireOp",EDGE,"E72")}),-1.0]])]});
            var Q15;
            Q15=makeQuery(id+"F12.imprint","IMPRINT",FACE,{"disambiguationData":[TD([[makeQuery(id+"F12.imprint","IMPRINT",EDGE,{"derivedFrom":sQuery(id+"F12.wireOp",EDGE,"E83")}),-1.0]])]});
            var Q16;
            Q16=makeQuery(id+"F12.imprint","IMPRINT",FACE,{"disambiguationData":[TD([[makeQuery(id+"F12.imprint","IMPRINT",EDGE,{"derivedFrom":sQuery(id+"F12.wireOp",EDGE,"E112")}),-1.0]])]});
            var Q17;
            Q17=makeQuery(id+"F12.imprint","IMPRINT",FACE,{"disambiguationData":[TD([[makeQuery(id+"F12.imprint","IMPRINT",EDGE,{"derivedFrom":sQuery(id+"F12.wireOp",EDGE,"E95")}),-1.0]])]});
            var Q18;
            Q18=makeQuery(id+"F12.imprint","IMPRINT",FACE,{"disambiguationData":[TD([[makeQuery(id+"F12.imprint","IMPRINT",EDGE,{"derivedFrom":sQuery(id+"F12.wireOp",EDGE,"E89")}),-1.0]])]});
            var Q19;
            Q19=makeQuery(id+"F12.imprint","IMPRINT",FACE,{"disambiguationData":[TD([[makeQuery(id+"F12.imprint","IMPRINT",EDGE,{"derivedFrom":sQuery(id+"F12.wireOp",EDGE,"E92")}),-1.0]])]});
            var Q20;
            Q20=makeQuery(id+"F12.imprint","IMPRINT",FACE,{"disambiguationData":[TD([[makeQuery(id+"F12.imprint","IMPRINT",EDGE,{"derivedFrom":sQuery(id+"F12.wireOp",EDGE,"E108")}),-1.0]])]});
            var Q21;
            Q21=makeQuery(id+"F12.imprint","IMPRINT",FACE,{"disambiguationData":[TD([[makeQuery(id+"F12.imprint","IMPRINT",EDGE,{"derivedFrom":sQuery(id+"F12.wireOp",EDGE,"E102")}),-1.0]])]});
            var Q22;
            Q22=makeQuery(id+"F12.imprint","IMPRINT",FACE,{"disambiguationData":[TD([[makeQuery(id+"F12.imprint","IMPRINT",EDGE,{"derivedFrom":sQuery(id+"F12.wireOp",EDGE,"E99")}),-1.0]])]});
            var Q23;
            Q23=makeQuery(id+"F12.imprint","IMPRINT",FACE,{"disambiguationData":[TD([[makeQuery(id+"F12.imprint","IMPRINT",EDGE,{"derivedFrom":sQuery(id+"F12.wireOp",EDGE,"E105")}),-1.0]])]});
            var Q24;
            Q24=makeQuery(id+"F12.imprint","IMPRINT",FACE,{"disambiguationData":[TD([[makeQuery(id+"F12.imprint","IMPRINT",EDGE,{"derivedFrom":sQuery(id+"F12.wireOp",EDGE,"E115")}),-1.0]])]});
            extrude(context, id + "F13", {"entities" : qUnion([Q0, Q1, Q2, Q3, Q4, Q5, Q6, Q7, Q8, Q9, Q10, Q11, Q12, Q13, Q14, Q15, Q16, Q17, Q18, Q19, Q20, Q21, Q22, Q23, Q24]), "operationType" : NewBodyOperationType.ADD, "depth" : 5 * mm, "offsetDistance" : 25 * mm});
        }
        {
            var Q0;
            Q0=makeQuery(id+"F12.imprint","IMPRINT",FACE,{"disambiguationData":[TD([[makeQuery(id+"F12.imprint","IMPRINT",EDGE,{"derivedFrom":sQuery(id+"F12.wireOp",EDGE,"E59")}),-1.0]])]});
            var Q1;
            Q1=makeQuery(id+"F12.imprint","IMPRINT",FACE,{"disambiguationData":[TD([[makeQuery(id+"F12.imprint","IMPRINT",EDGE,{"derivedFrom":sQuery(id+"F12.wireOp",EDGE,"af930993-f983-4d4b-806c-d5d714f01deb")}),-1.0]])]});
            var Q2;
            Q2=makeQuery(id+"F12.imprint","IMPRINT",FACE,{"disambiguationData":[TD([[makeQuery(id+"F12.imprint","IMPRINT",EDGE,{"derivedFrom":sQuery(id+"F12.wireOp",EDGE,"544cc5c5-56e9-462e-aa7d-0e891712fb88")}),-1.0]])]});
            var Q3;
            Q3=makeQuery(id+"F12.imprint","IMPRINT",FACE,{"disambiguationData":[TD([[makeQuery(id+"F12.imprint","IMPRINT",EDGE,{"derivedFrom":sQuery(id+"F12.wireOp",EDGE,"a7fd36b7-951d-469d-bd4a-abdf8a5abec4")}),-1.0]])]});
            var Q4;
            Q4=makeQuery(id+"F12.imprint","IMPRINT",FACE,{"disambiguationData":[TD([[makeQuery(id+"F12.imprint","IMPRINT",EDGE,{"derivedFrom":sQuery(id+"F12.wireOp",EDGE,"db4000d2-28b7-4ce0-b6f8-efe2c8e47721")}),-1.0]])]});
            var Q5;
            Q5=makeQuery(id+"F12.imprint","IMPRINT",FACE,{"disambiguationData":[TD([[makeQuery(id+"F12.imprint","IMPRINT",EDGE,{"derivedFrom":sQuery(id+"F12.wireOp",EDGE,"6fd45c98-9014-41e2-a4b9-07c20c1fc8f4")}),-1.0]])]});
            var Q6;
            Q6=makeQuery(id+"F12.imprint","IMPRINT",FACE,{"disambiguationData":[TD([[makeQuery(id+"F12.imprint","IMPRINT",EDGE,{"derivedFrom":sQuery(id+"F12.wireOp",EDGE,"0217be3f-f015-4376-87de-3fac7a7125e00.MirrorCS")}),1.0]])]});
            var Q7;
            Q7=makeQuery(id+"F12.imprint","IMPRINT",FACE,{"disambiguationData":[TD([[makeQuery(id+"F12.imprint","IMPRINT",EDGE,{"derivedFrom":sQuery(id+"F12.wireOp",EDGE,"3a05cbfe-0b2f-41ad-9fce-b7c3e8f461170.MirrorCS")}),1.0]])]});
            var Q8;
            Q8=makeQuery(id+"F12.imprint","IMPRINT",FACE,{"disambiguationData":[TD([[makeQuery(id+"F12.imprint","IMPRINT",EDGE,{"derivedFrom":sQuery(id+"F12.wireOp",EDGE,"686798c7-8504-4800-9966-571d6854760d0.MirrorCS")}),1.0]])]});
            var Q9;
            Q9=makeQuery(id+"F12.imprint","IMPRINT",FACE,{"disambiguationData":[TD([[makeQuery(id+"F12.imprint","IMPRINT",EDGE,{"derivedFrom":sQuery(id+"F12.wireOp",EDGE,"ee1293b9-60a1-4feb-baa6-848b5ec06ea80.MirrorCS")}),1.0]])]});
            var Q10;
            Q10=makeQuery(id+"F12.imprint","IMPRINT",FACE,{"disambiguationData":[TD([[makeQuery(id+"F12.imprint","IMPRINT",EDGE,{"derivedFrom":sQuery(id+"F12.wireOp",EDGE,"E83")}),-1.0]])]});
            var Q11;
            Q11=makeQuery(id+"F12.imprint","IMPRINT",FACE,{"disambiguationData":[TD([[makeQuery(id+"F12.imprint","IMPRINT",EDGE,{"derivedFrom":sQuery(id+"F12.wireOp",EDGE,"E72")}),-1.0]])]});
            var Q12;
            Q12=makeQuery(id+"F12.imprint","IMPRINT",FACE,{"disambiguationData":[TD([[makeQuery(id+"F12.imprint","IMPRINT",EDGE,{"derivedFrom":sQuery(id+"F12.wireOp",EDGE,"E78")}),-1.0]])]});
            var Q13;
            Q13=makeQuery(id+"F12.imprint","IMPRINT",FACE,{"disambiguationData":[TD([[makeQuery(id+"F12.imprint","IMPRINT",EDGE,{"derivedFrom":sQuery(id+"F12.wireOp",EDGE,"E75")}),-1.0]])]});
            var Q14;
            Q14=makeQuery(id+"F12.imprint","IMPRINT",FACE,{"disambiguationData":[TD([[makeQuery(id+"F12.imprint","IMPRINT",EDGE,{"derivedFrom":sQuery(id+"F12.wireOp",EDGE,"E86")}),-1.0]])]});
            var Q15;
            Q15=makeQuery(id+"F12.imprint","IMPRINT",FACE,{"disambiguationData":[TD([[makeQuery(id+"F12.imprint","IMPRINT",EDGE,{"derivedFrom":sQuery(id+"F12.wireOp",EDGE,"E115")}),-1.0]])]});
            var Q16;
            Q16=makeQuery(id+"F12.imprint","IMPRINT",FACE,{"disambiguationData":[TD([[makeQuery(id+"F12.imprint","IMPRINT",EDGE,{"derivedFrom":sQuery(id+"F12.wireOp",EDGE,"E105")}),-1.0]])]});
            var Q17;
            Q17=makeQuery(id+"F12.imprint","IMPRINT",FACE,{"disambiguationData":[TD([[makeQuery(id+"F12.imprint","IMPRINT",EDGE,{"derivedFrom":sQuery(id+"F12.wireOp",EDGE,"E99")}),-1.0]])]});
            var Q18;
            Q18=makeQuery(id+"F12.imprint","IMPRINT",FACE,{"disambiguationData":[TD([[makeQuery(id+"F12.imprint","IMPRINT",EDGE,{"derivedFrom":sQuery(id+"F12.wireOp",EDGE,"E102")}),-1.0]])]});
            var Q19;
            Q19=makeQuery(id+"F12.imprint","IMPRINT",FACE,{"disambiguationData":[TD([[makeQuery(id+"F12.imprint","IMPRINT",EDGE,{"derivedFrom":sQuery(id+"F12.wireOp",EDGE,"E108")}),-1.0]])]});
            var Q20;
            Q20=makeQuery(id+"F12.imprint","IMPRINT",FACE,{"disambiguationData":[TD([[makeQuery(id+"F12.imprint","IMPRINT",EDGE,{"derivedFrom":sQuery(id+"F12.wireOp",EDGE,"E92")}),-1.0]])]});
            var Q21;
            Q21=makeQuery(id+"F12.imprint","IMPRINT",FACE,{"disambiguationData":[TD([[makeQuery(id+"F12.imprint","IMPRINT",EDGE,{"derivedFrom":sQuery(id+"F12.wireOp",EDGE,"E89")}),-1.0]])]});
            var Q22;
            Q22=makeQuery(id+"F12.imprint","IMPRINT",FACE,{"disambiguationData":[TD([[makeQuery(id+"F12.imprint","IMPRINT",EDGE,{"derivedFrom":sQuery(id+"F12.wireOp",EDGE,"E95")}),-1.0]])]});
            var Q23;
            Q23=makeQuery(id+"F12.imprint","IMPRINT",FACE,{"disambiguationData":[TD([[makeQuery(id+"F12.imprint","IMPRINT",EDGE,{"derivedFrom":sQuery(id+"F12.wireOp",EDGE,"E112")}),-1.0]])]});
            extrude(context, id + "F14", {"entities" : qUnion([Q0, Q1, Q2, Q3, Q4, Q5, Q6, Q7, Q8, Q9, Q10, Q11, Q12, Q13, Q14, Q15, Q16, Q17, Q18, Q19, Q20, Q21, Q22, Q23]), "operationType" : NewBodyOperationType.REMOVE, "depth" : 3 * mm, "offsetDistance" : 25 * mm});
        }
    });
